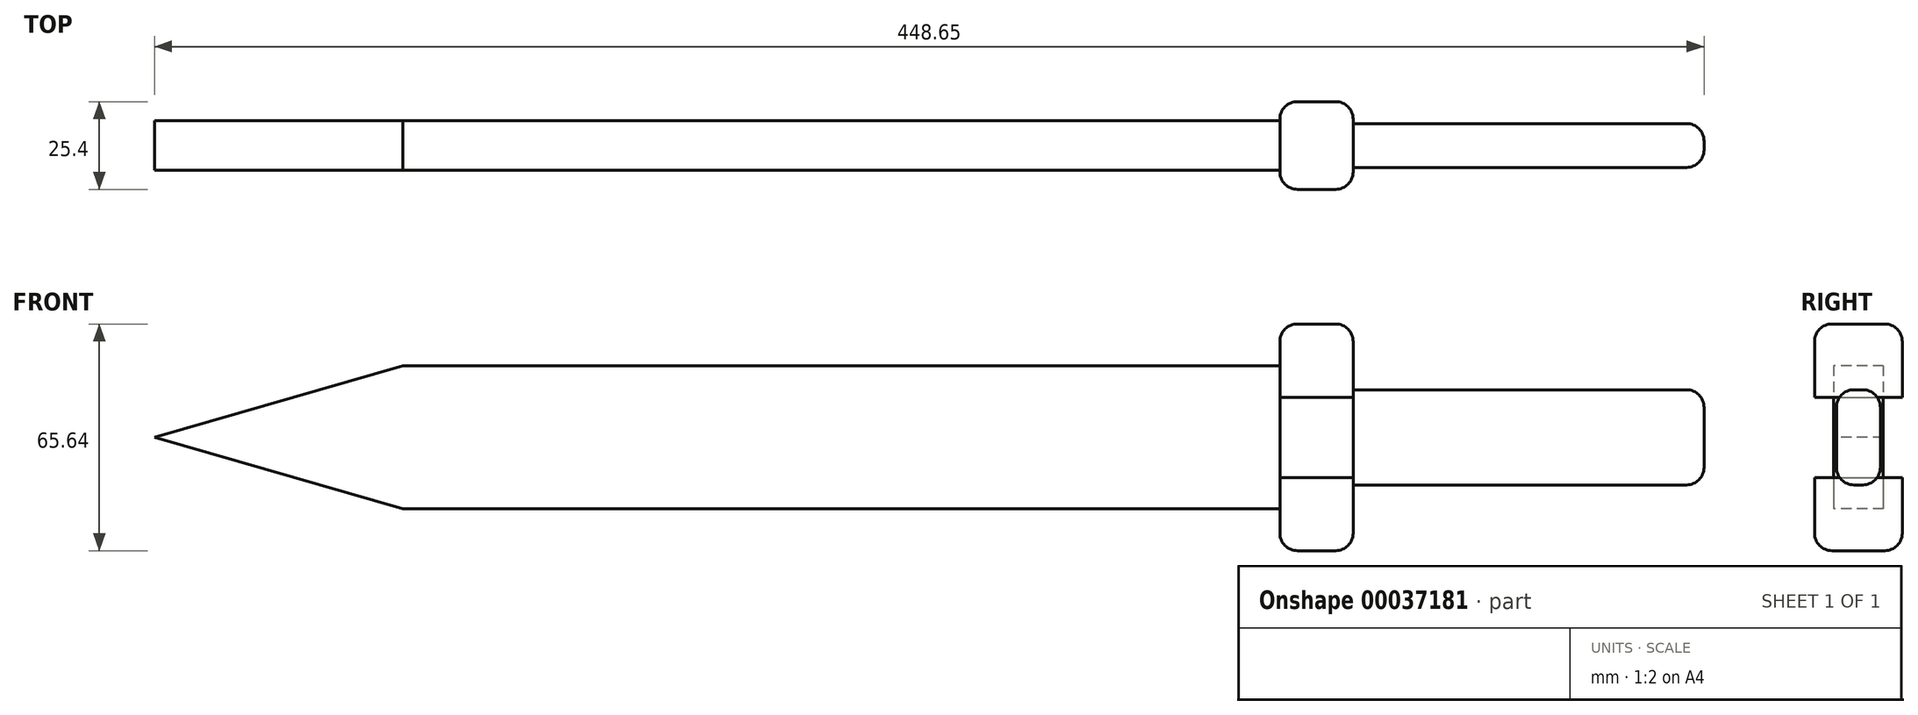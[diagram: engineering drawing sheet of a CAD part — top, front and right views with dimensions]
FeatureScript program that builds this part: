
annotation { "Feature Type Name" : "Feature", "Feature Type Description" : "" }
export const myFeature = defineFeature(function(context is Context, id is Id, definition is map)
    precondition{}
    {
        {
            var Q0;
            Q0=qCreatedBy(makeId("Front.planeOp"),FACE);
            var sketch = newSketch(context, id + "F0", { "sketchPlane" : qUnion([Q0])});
            skLineSegment(sketch, "E0.left", {"start": v(0, 0) * mm, "end": v(0, 23.24) * mm});
            skLineSegment(sketch, "E1.bottom", {"start": v(0, 23.24) * mm, "end": v(21.2, 23.24) * mm});
            skLineSegment(sketch, "E1.top", {"start": v(0, 0) * mm, "end": v(21.2, 0) * mm});
            skLineSegment(sketch, "E1.left", {"start": v(0, 23.24) * mm, "end": v(0, 0) * mm});
            skLineSegment(sketch, "E1.right", {"start": v(21.2, 23.24) * mm, "end": v(21.2, 0) * mm});
            skLineSegment(sketch, "E2.bottom", {"start": v(0, 44.44) * mm, "end": v(21.2, 44.44) * mm});
            skLineSegment(sketch, "E2.left", {"start": v(0, 44.44) * mm, "end": v(0, 23.24) * mm});
            skLineSegment(sketch, "E2.right", {"start": v(21.2, 44.44) * mm, "end": v(21.2, 23.24) * mm});
            skLineSegment(sketch, "E3.bottom", {"start": v(0, -21.2) * mm, "end": v(21.2, -21.2) * mm});
            skLineSegment(sketch, "E3.left", {"start": v(0, -21.2) * mm, "end": v(0, 0) * mm});
            skLineSegment(sketch, "E3.right", {"start": v(21.2, -21.2) * mm, "end": v(21.2, 0) * mm});
            skSolve(sketch);
        }
        {
            var Q0;
            Q0=makeQuery(id+"F0.imprint","IMPRINT",FACE,{"disambiguationData":[TD([[makeQuery(id+"F0.imprint","IMPRINT",EDGE,{"derivedFrom":sQuery(id+"F0.wireOp",EDGE,"E2.bottom")}),-1.0]])]});
            var Q1;
            Q1=makeQuery(id+"F0.imprint","IMPRINT",FACE,{"disambiguationData":[TD([[makeQuery(id+"F0.imprint","IMPRINT",EDGE,{"derivedFrom":sQuery(id+"F0.wireOp",EDGE,"E3.bottom")}),1.0]])]});
            var Q2;
            Q2=makeQuery(id+"F0.imprint","IMPRINT",FACE,{"disambiguationData":[TD([[makeQuery(id+"F0.imprint","IMPRINT",EDGE,{"derivedFrom":sQuery(id+"F0.wireOp",EDGE,"E1.left")}),1.0]])]});
            extrude(context, id + "F1", {"entities" : qUnion([Q0, Q1, Q2]), "depth" : 25.4 * mm});
        }
        {
            var Q0;
            Q0=makeQuery(id+"F1.opExtrude","SWEPT_FACE",FACE,{"disambiguationData":[OSD([sQuery(id+"F0.wireOp",EDGE,"E2.right"),sQuery(id+"F0.wireOp",EDGE,"E3.right"),sQuery(id+"F0.wireOp",EDGE,"E1.right")])]});
            var sketch = newSketch(context, id + "F2", { "sketchPlane" : qUnion([Q0])});
            skLineSegment(sketch, "E4.bottom", {"start": v(-19.05, 25.4) * mm, "end": v(-6.35, 25.4) * mm});
            skLineSegment(sketch, "E4.top", {"start": v(-19.05, -2.15) * mm, "end": v(-6.35, -2.15) * mm});
            skLineSegment(sketch, "E4.left", {"start": v(-19.05, 25.4) * mm, "end": v(-19.05, -2.15) * mm});
            skLineSegment(sketch, "E4.right", {"start": v(-6.35, 25.4) * mm, "end": v(-6.35, -2.15) * mm});
            skSolve(sketch);
        }
        {
            var Q0;
            Q0 = qSketchRegion(id + "F2", true);
            extrude(context, id + "F3", {"entities" : qUnion([Q0]), "operationType" : NewBodyOperationType.ADD, "depth" : 101.6 * mm});
        }
        {
            var Q0;
            Q0=makeQuery(id+"F1.opExtrude","SWEPT_FACE",FACE,{"disambiguationData":[OSD([sQuery(id+"F0.wireOp",EDGE,"E1.left"),sQuery(id+"F0.wireOp",EDGE,"E2.left"),sQuery(id+"F0.wireOp",EDGE,"E3.left")])]});
            var sketch = newSketch(context, id + "F4", { "sketchPlane" : qUnion([Q0])});
            skLineSegment(sketch, "E5.bottom", {"start": v(5.51, 32.35) * mm, "end": v(19.89, 32.35) * mm});
            skLineSegment(sketch, "E5.top", {"start": v(5.51, -9.11) * mm, "end": v(19.89, -9.11) * mm});
            skLineSegment(sketch, "E5.left", {"start": v(5.51, 32.35) * mm, "end": v(5.51, -9.11) * mm});
            skLineSegment(sketch, "E5.right", {"start": v(19.89, 32.35) * mm, "end": v(19.89, -9.11) * mm});
            skSolve(sketch);
        }
        {
            var Q0;
            Q0 = qSketchRegion(id + "F4", true);
            extrude(context, id + "F5", {"entities" : qUnion([Q0]), "operationType" : NewBodyOperationType.ADD, "depth" : 254 * mm});
        }
        {
            var Q0;
            Q0=makeQuery(id+"F5.opExtrude","SWEPT_FACE",FACE,{"disambiguationData":[OSD([sQuery(id+"F4.wireOp",EDGE,"E5.right")])]});
            var sketch = newSketch(context, id + "F6", { "sketchPlane" : qUnion([Q0])});
            skLineSegment(sketch, "E6", {"start": v(-254, 32.35) * mm, "end": v(-325.85, 11.62) * mm});
            skPoint(sketch, "E6.endSnap0", {"position": v(-254, 11.62) * mm});
            skLineSegment(sketch, "E7", {"start": v(-325.85, 11.62) * mm, "end": v(-254, -9.11) * mm});
            skSolve(sketch);
        }
        {
            var Q0;
            Q0=makeQuery(id+"F6.imprint","IMPRINT",FACE,{"disambiguationData":[TD([[makeQuery(id+"F6.imprint","IMPRINT",EDGE,{"derivedFrom":sQuery(id+"F6.wireOp",EDGE,"E6")}),1.0]])]});
            extrude(context, id + "F7", {"entities" : qUnion([Q0]), "operationType" : NewBodyOperationType.ADD, "oppositeDirection" : true, "depth" : 14.38 * mm});
        }
        {
            var Q0;
            Q0=makeQuery(id+"F1.opExtrude","CAP_EDGE",EDGE,{"disambiguationData":[OSD([sQuery(id+"F0.wireOp",EDGE,"E2.right"),sQuery(id+"F0.wireOp",EDGE,"E3.right"),sQuery(id+"F0.wireOp",EDGE,"E1.right")])],"isStart":false});
            var Q1;
            Q1=makeQuery(id+"F1.opExtrude","CAP_EDGE",EDGE,{"disambiguationData":[OSD([sQuery(id+"F0.wireOp",EDGE,"E1.left"),sQuery(id+"F0.wireOp",EDGE,"E2.left"),sQuery(id+"F0.wireOp",EDGE,"E3.left")])],"isStart":false});
            var Q2;
            Q2=makeQuery(id+"F1.opExtrude","CAP_EDGE",EDGE,{"disambiguationData":[OSD([sQuery(id+"F0.wireOp",EDGE,"E1.left"),sQuery(id+"F0.wireOp",EDGE,"E2.left"),sQuery(id+"F0.wireOp",EDGE,"E3.left")])],"isStart":true});
            var Q3;
            Q3=makeQuery(id+"F1.opExtrude","CAP_EDGE",EDGE,{"disambiguationData":[OSD([sQuery(id+"F0.wireOp",EDGE,"E2.right"),sQuery(id+"F0.wireOp",EDGE,"E3.right"),sQuery(id+"F0.wireOp",EDGE,"E1.right")])],"isStart":true});
            var Q4;
            Q4=makeQuery(id+"F1.opExtrude","CAP_EDGE",EDGE,{"disambiguationData":[OSD([sQuery(id+"F0.wireOp",EDGE,"E2.bottom")])],"isStart":false});
            var Q5;
            Q5=makeQuery(id+"F1.opExtrude","SWEPT_EDGE",EDGE,{"disambiguationData":[OSD([sQuery(id+"F0.wireOp",EDGE,"E2.bottom"),sQuery(id+"F0.wireOp",EDGE,"E2.right")])]});
            var Q6;
            Q6=makeQuery(id+"F1.opExtrude","CAP_EDGE",EDGE,{"disambiguationData":[OSD([sQuery(id+"F0.wireOp",EDGE,"E2.bottom")])],"isStart":true});
            var Q7;
            Q7=makeQuery(id+"F1.opExtrude","SWEPT_EDGE",EDGE,{"disambiguationData":[OSD([sQuery(id+"F0.wireOp",EDGE,"E2.bottom"),sQuery(id+"F0.wireOp",EDGE,"E2.left")])]});
            var Q8;
            Q8=makeQuery(id+"F1.opExtrude","CAP_EDGE",EDGE,{"disambiguationData":[OSD([sQuery(id+"F0.wireOp",EDGE,"E3.bottom")])],"isStart":false});
            var Q9;
            Q9=makeQuery(id+"F1.opExtrude","SWEPT_EDGE",EDGE,{"disambiguationData":[OSD([sQuery(id+"F0.wireOp",EDGE,"E3.bottom"),sQuery(id+"F0.wireOp",EDGE,"E3.right")])]});
            var Q10;
            Q10=makeQuery(id+"F1.opExtrude","SWEPT_EDGE",EDGE,{"disambiguationData":[OSD([sQuery(id+"F0.wireOp",EDGE,"E3.bottom"),sQuery(id+"F0.wireOp",EDGE,"E3.left")])]});
            var Q11;
            Q11=makeQuery(id+"F1.opExtrude","CAP_EDGE",EDGE,{"disambiguationData":[OSD([sQuery(id+"F0.wireOp",EDGE,"E3.bottom")])],"isStart":true});
            var Q12;
            Q12=makeQuery(id+"F3.opExtrude","CAP_EDGE",EDGE,{"disambiguationData":[OSD([sQuery(id+"F2.wireOp",EDGE,"E4.left")])],"isStart":false});
            var Q13;
            Q13=makeQuery(id+"F3.opExtrude","CAP_EDGE",EDGE,{"disambiguationData":[OSD([sQuery(id+"F2.wireOp",EDGE,"E4.right")])],"isStart":false});
            var Q14;
            Q14=makeQuery(id+"F3.opExtrude","CAP_EDGE",EDGE,{"disambiguationData":[OSD([sQuery(id+"F2.wireOp",EDGE,"E4.top")])],"isStart":false});
            var Q15;
            Q15=makeQuery(id+"F3.opExtrude","CAP_EDGE",EDGE,{"disambiguationData":[OSD([sQuery(id+"F2.wireOp",EDGE,"E4.bottom")])],"isStart":false});
            var Q16;
            Q16=makeQuery(id+"F3.opExtrude","SWEPT_EDGE",EDGE,{"disambiguationData":[OSD([sQuery(id+"F2.wireOp",EDGE,"E4.bottom"),sQuery(id+"F2.wireOp",EDGE,"E4.left")])]});
            var Q17;
            Q17=makeQuery(id+"F3.opExtrude","SWEPT_EDGE",EDGE,{"disambiguationData":[OSD([sQuery(id+"F2.wireOp",EDGE,"E4.bottom"),sQuery(id+"F2.wireOp",EDGE,"E4.right")])]});
            var Q18;
            Q18=makeQuery(id+"F3.opExtrude","SWEPT_EDGE",EDGE,{"disambiguationData":[OSD([sQuery(id+"F2.wireOp",EDGE,"E4.top"),sQuery(id+"F2.wireOp",EDGE,"E4.left")])]});
            var Q19;
            Q19=makeQuery(id+"F3.opExtrude","SWEPT_EDGE",EDGE,{"disambiguationData":[OSD([sQuery(id+"F2.wireOp",EDGE,"E4.top"),sQuery(id+"F2.wireOp",EDGE,"E4.right")])]});
            fillet(context, id + "F8", {"entities" : qUnion([Q0, Q1, Q2, Q3, Q4, Q5, Q6, Q7, Q8, Q9, Q10, Q11, Q12, Q13, Q14, Q15, Q16, Q17, Q18, Q19]), "radius" : 5.08 * mm, "tangentPropagation" : true, "allowEdgeOverflow" : false});
        }
    });
